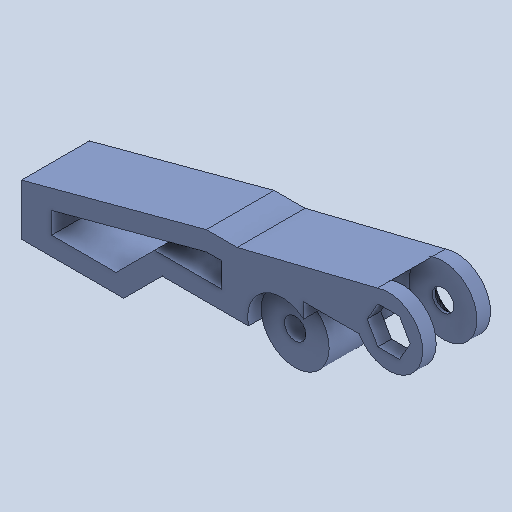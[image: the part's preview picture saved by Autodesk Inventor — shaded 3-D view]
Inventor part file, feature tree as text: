
AUTODESK INVENTOR PART (.ipt)
format: ipt  version: 2025.2 (Build 292293000, 293)  size: 167,936 bytes
history: native  units: mm
features: other x4, sketch x4
ambient origin geometry x8: Origin, YZ Plane, XZ Plane, XY Plane, X Axis, Y Axis, Z Axis, Center Point
bodies: Body1 (feature_tree)
feature tree (8):
  other  "Pinza_0002_001.ipt"
  other  "Sólido1::Pinza_0002_001.ipt"
  other  "OperaçãoIdentificador1"
  sketch  "Esboço1"  dims[d0=10.0mm]
  sketch  "Esboço2"
  sketch  "Esboço3"
  sketch  "Esboço4"
  other  "Sólido1"
